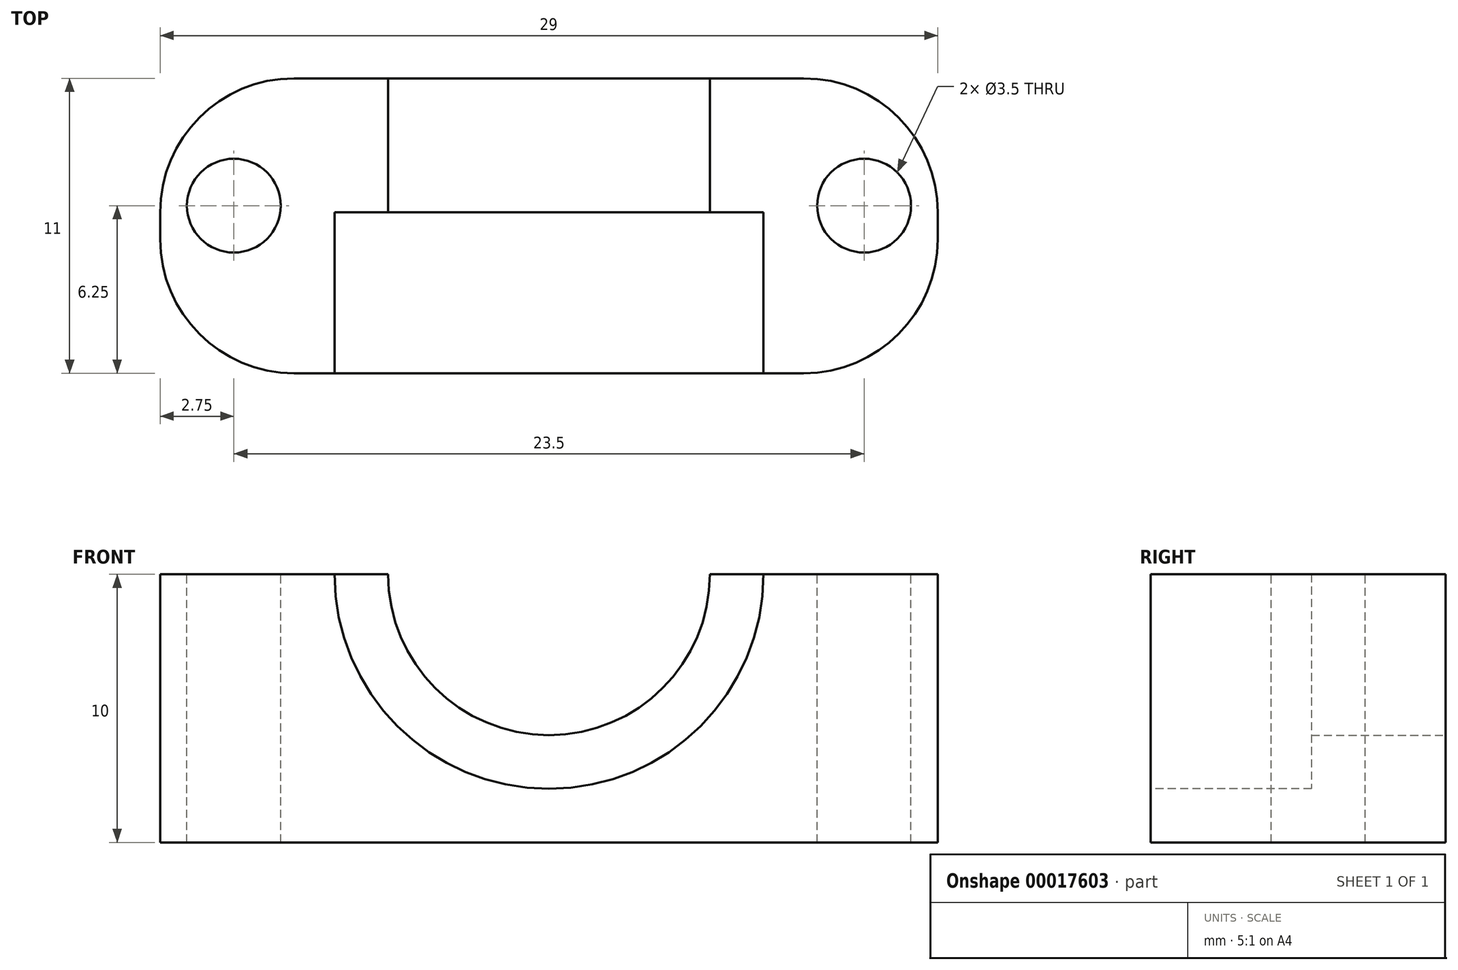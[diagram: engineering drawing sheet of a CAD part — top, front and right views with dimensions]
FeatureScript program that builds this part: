
annotation { "Feature Type Name" : "Feature", "Feature Type Description" : "" }
export const myFeature = defineFeature(function(context is Context, id is Id, definition is map)
    precondition{}
    {
        {
            var Q0;
            Q0=qCreatedBy(makeId("Top.planeOp"),FACE);
            var sketch = newSketch(context, id + "F0", { "sketchPlane" : qUnion([Q0])});
            skLineSegment(sketch, "E0.bottom", {"start": v(0, 0) * mm, "end": v(25, 0) * mm});
            skLineSegment(sketch, "E0.top", {"start": v(0, 11) * mm, "end": v(25, 11) * mm});
            skLineSegment(sketch, "E0.left", {"start": v(0, 0) * mm, "end": v(0, 11) * mm});
            skLineSegment(sketch, "E0.right", {"start": v(25, 0) * mm, "end": v(25, 11) * mm});
            skSolve(sketch);
        }
        {
            var Q0;
            Q0=qSketchRegion(id+"F0",true);
            extrude(context, id + "F1", {"entities" : qUnion([Q0]), "depth" : 10 * mm});
        }
        {
            var Q0;
            Q0=makeQuery(id+"F1.opExtrude","SWEPT_FACE",FACE,{"disambiguationData":[OSD([sQuery(id+"F0.wireOp",EDGE,"E0.bottom")])]});
            var sketch = newSketch(context, id + "F2", { "sketchPlane" : qUnion([Q0])});
            skCircle(sketch, "E1", {"center": v(12.5, 10) * mm, "radius": 8 * mm});
            skSolve(sketch);
        }
        {
            var Q0;
            Q0=qSketchRegion(id+"F2",true);
            extrude(context, id + "F3", {"entities" : qUnion([Q0]), "operationType" : NewBodyOperationType.REMOVE, "oppositeDirection" : true, "depth" : 6 * mm});
        }
        {
            var Q0;
            Q0=makeQuery(id+"F1.opExtrude","SWEPT_FACE",FACE,{"disambiguationData":[OSD([sQuery(id+"F0.wireOp",EDGE,"E0.top")])]});
            var sketch = newSketch(context, id + "F4", { "sketchPlane" : qUnion([Q0])});
            skCircle(sketch, "E2", {"center": v(-12.5, 10) * mm, "radius": 6 * mm});
            skSolve(sketch);
        }
        {
            var Q0;
            Q0=qSketchRegion(id+"F4",true);
            extrude(context, id + "F5", {"entities" : qUnion([Q0]), "operationType" : NewBodyOperationType.REMOVE, "oppositeDirection" : true, "depth" : 6 * mm});
        }
        {
            var Q0;
            Q0=makeQuery(id+"F1.opExtrude","SWEPT_FACE",FACE,{"disambiguationData":[OSD([sQuery(id+"F0.wireOp",EDGE,"E0.left")])]});
            var sketch = newSketch(context, id + "F6", { "sketchPlane" : qUnion([Q0])});
            skLineSegment(sketch, "E3.bottom", {"start": v(-11, 0) * mm, "end": v(0, 0) * mm});
            skLineSegment(sketch, "E3.top", {"start": v(-11, 10) * mm, "end": v(0, 10) * mm});
            skLineSegment(sketch, "E3.left", {"start": v(-11, 0) * mm, "end": v(-11, 10) * mm});
            skLineSegment(sketch, "E3.right", {"start": v(0, 0) * mm, "end": v(0, 10) * mm});
            skSolve(sketch);
        }
        {
            var Q0;
            Q0=qSketchRegion(id+"F6",true);
            extrude(context, id + "F7", {"entities" : qUnion([Q0]), "operationType" : NewBodyOperationType.ADD, "depth" : 2 * mm});
        }
        {
            var Q0;
            Q0=makeQuery(id+"F1.opExtrude","SWEPT_FACE",FACE,{"disambiguationData":[OSD([sQuery(id+"F0.wireOp",EDGE,"E0.right")])]});
            var sketch = newSketch(context, id + "F8", { "sketchPlane" : qUnion([Q0])});
            skLineSegment(sketch, "E4.bottom", {"start": v(11, 10) * mm, "end": v(0, 10) * mm});
            skLineSegment(sketch, "E4.top", {"start": v(11, 0) * mm, "end": v(0, 0) * mm});
            skLineSegment(sketch, "E4.left", {"start": v(11, 10) * mm, "end": v(11, 0) * mm});
            skLineSegment(sketch, "E4.right", {"start": v(0, 10) * mm, "end": v(0, 0) * mm});
            skSolve(sketch);
        }
        {
            var Q0;
            Q0=qSketchRegion(id+"F8",true);
            extrude(context, id + "F9", {"entities" : qUnion([Q0]), "operationType" : NewBodyOperationType.ADD, "depth" : 2 * mm});
        }
        {
            var Q0;
            Q0=makeQuery(id+"F9.opExtrude","CAP_EDGE",EDGE,{"disambiguationData":[OSD([sQuery(id+"F8.wireOp",EDGE,"E4.left")])],"isStart":false});
            var Q1;
            Q1=makeQuery(id+"F9.opExtrude","CAP_EDGE",EDGE,{"disambiguationData":[OSD([sQuery(id+"F8.wireOp",EDGE,"E4.right")])],"isStart":false});
            var Q2;
            Q2=makeQuery(id+"F7.opExtrude","CAP_EDGE",EDGE,{"disambiguationData":[OSD([sQuery(id+"F6.wireOp",EDGE,"E3.left")])],"isStart":false});
            var Q3;
            Q3=makeQuery(id+"F7.opExtrude","CAP_EDGE",EDGE,{"disambiguationData":[OSD([sQuery(id+"F6.wireOp",EDGE,"E3.right")])],"isStart":false});
            fillet(context, id + "F10", {"entities" : qUnion([Q0, Q1, Q2, Q3]), "radius" : 5 * mm, "tangentPropagation" : true, "allowEdgeOverflow" : false});
        }
        {
            var Q0;
            {var subQ0=sQuery(id+"F0.wireOp",EDGE,"E0.bottom");var subQ1=sQuery(id+"F0.wireOp",EDGE,"E0.top");var subQ2=sQuery(id+"F0.wireOp",EDGE,"E0.left");Q0=makeQuery(id+"F5.boolean.opBoolean","SPLIT",FACE,{"disambiguationData":[TD([makeQuery(id+"F1.opExtrude","SWEPT_FACE",FACE,{"disambiguationData":[OSD([subQ2])]})])],"derivedFrom":makeQuery(id+"F1.opExtrude","CAP_FACE",FACE,{"disambiguationData":[OSD([subQ0,subQ1,subQ2,sQuery(id+"F0.wireOp",EDGE,"E0.right")])],"isStart":false})});}
            var sketch = newSketch(context, id + "F11", { "sketchPlane" : qUnion([Q0])});
            skCircle(sketch, "E5", {"center": v(0.75, 6.25) * mm, "radius": 1.75 * mm});
            skCircle(sketch, "E6", {"center": v(24.25, 6.25) * mm, "radius": 1.75 * mm});
            skSolve(sketch);
        }
        {
            var Q0;
            Q0=qSketchRegion(id+"F11",true);
            extrude(context, id + "F12", {"entities" : qUnion([Q0]), "operationType" : NewBodyOperationType.REMOVE, "oppositeDirection" : true, "depth" : 25 * mm});
        }
    });
